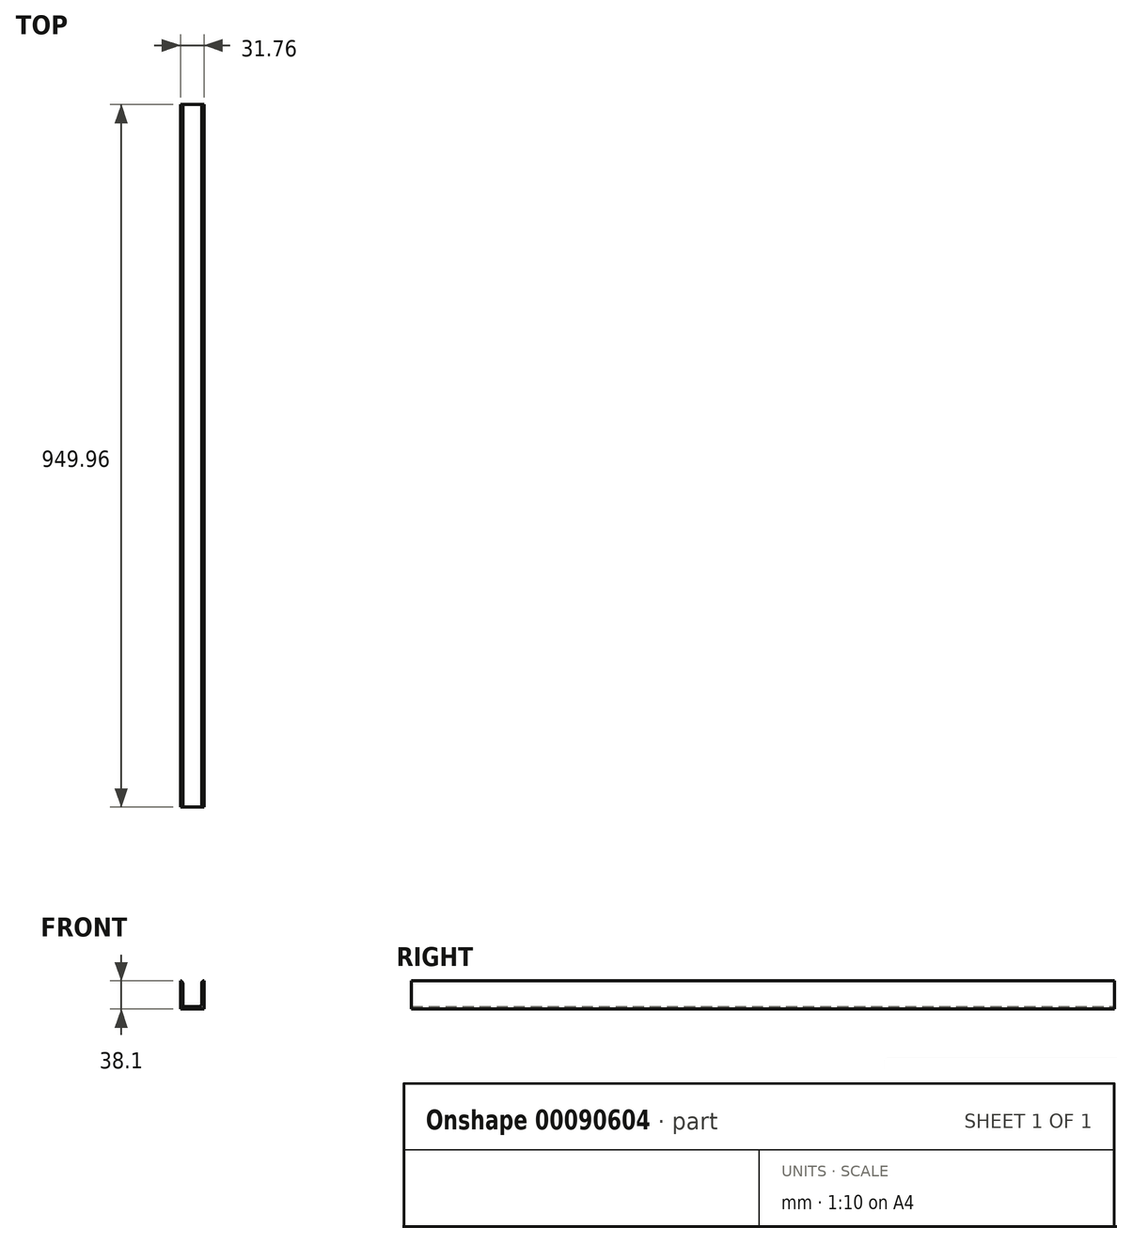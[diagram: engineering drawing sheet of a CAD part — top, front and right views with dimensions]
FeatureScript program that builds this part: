
annotation { "Feature Type Name" : "Feature", "Feature Type Description" : "" }
export const myFeature = defineFeature(function(context is Context, id is Id, definition is map)
    precondition{}
    {
        {
            var Q0;
            Q0=qCreatedBy(makeId("Front.planeOp"),FACE);
            var sketch = newSketch(context, id + "F0", { "sketchPlane" : qUnion([Q0])});
            skLineSegment(sketch, "E0.bottom", {"start": v(15.87, 19.05) * mm, "end": v(15.87, 19.05) * mm});
            skLineSegment(sketch, "E0.top", {"start": v(15.88, -19.05) * mm, "end": v(-15.87, -19.05) * mm});
            skLineSegment(sketch, "E0.left", {"start": v(15.87, 19.05) * mm, "end": v(15.88, -19.05) * mm});
            skLineSegment(sketch, "E0.right", {"start": v(-15.88, 19.05) * mm, "end": v(-15.87, -19.05) * mm});
            skPoint(sketch, "E0.middle", {"position": v(0, 0) * mm});
            skLineSegment(sketch, "E1.top", {"start": v(-9.52, -15.88) * mm, "end": v(9.53, -15.88) * mm});
            skLineSegment(sketch, "E1.left", {"start": v(-12.7, 15.87) * mm, "end": v(-12.7, -12.7) * mm});
            skLineSegment(sketch, "E1.right", {"start": v(12.7, 15.88) * mm, "end": v(12.7, -12.7) * mm});
            skLineSegment(sketch, "E2", {"start": v(-12.7, 15.87) * mm, "end": v(-12.7, 15.87) * mm});
            skLineSegment(sketch, "E3", {"start": v(12.7, 15.88) * mm, "end": v(12.7, 15.87) * mm});
            skLineSegment(sketch, "E4.trimOffspring", {"start": v(-15.88, 19.05) * mm, "end": v(-15.88, 19.05) * mm});
            skPoint(sketch, "E5.visualSharp", {"position": v(-12.7, 19.05) * mm});
            skArc(sketch, "E5.filletArc", {"start": v(-12.7, 15.87) * mm, "mid": v(-13.63, 18.12) * mm, "end": v(-15.88, 19.05) * mm});
            skPoint(sketch, "E6.visualSharp", {"position": v(12.7, 19.05) * mm});
            skArc(sketch, "E6.filletArc", {"start": v(15.87, 19.05) * mm, "mid": v(13.63, 18.12) * mm, "end": v(12.7, 15.87) * mm});
            skPoint(sketch, "E7.visualSharp", {"position": v(12.7, -15.87) * mm});
            skArc(sketch, "E7.filletArc", {"start": v(9.53, -15.88) * mm, "mid": v(11.77, -14.95) * mm, "end": v(12.7, -12.7) * mm});
            skPoint(sketch, "E8.visualSharp", {"position": v(-12.7, -15.88) * mm});
            skArc(sketch, "E8.filletArc", {"start": v(-12.7, -12.7) * mm, "mid": v(-11.77, -14.95) * mm, "end": v(-9.52, -15.88) * mm});
            skSolve(sketch);
        }
        {
            var Q0;
            Q0 = qSketchRegion(id + "F0", true);
            extrude(context, id + "F1", {"entities" : qUnion([Q0]), "endBound" : BoundingType.SYMMETRIC, "depth" : 949.96 * mm});
        }
    });
